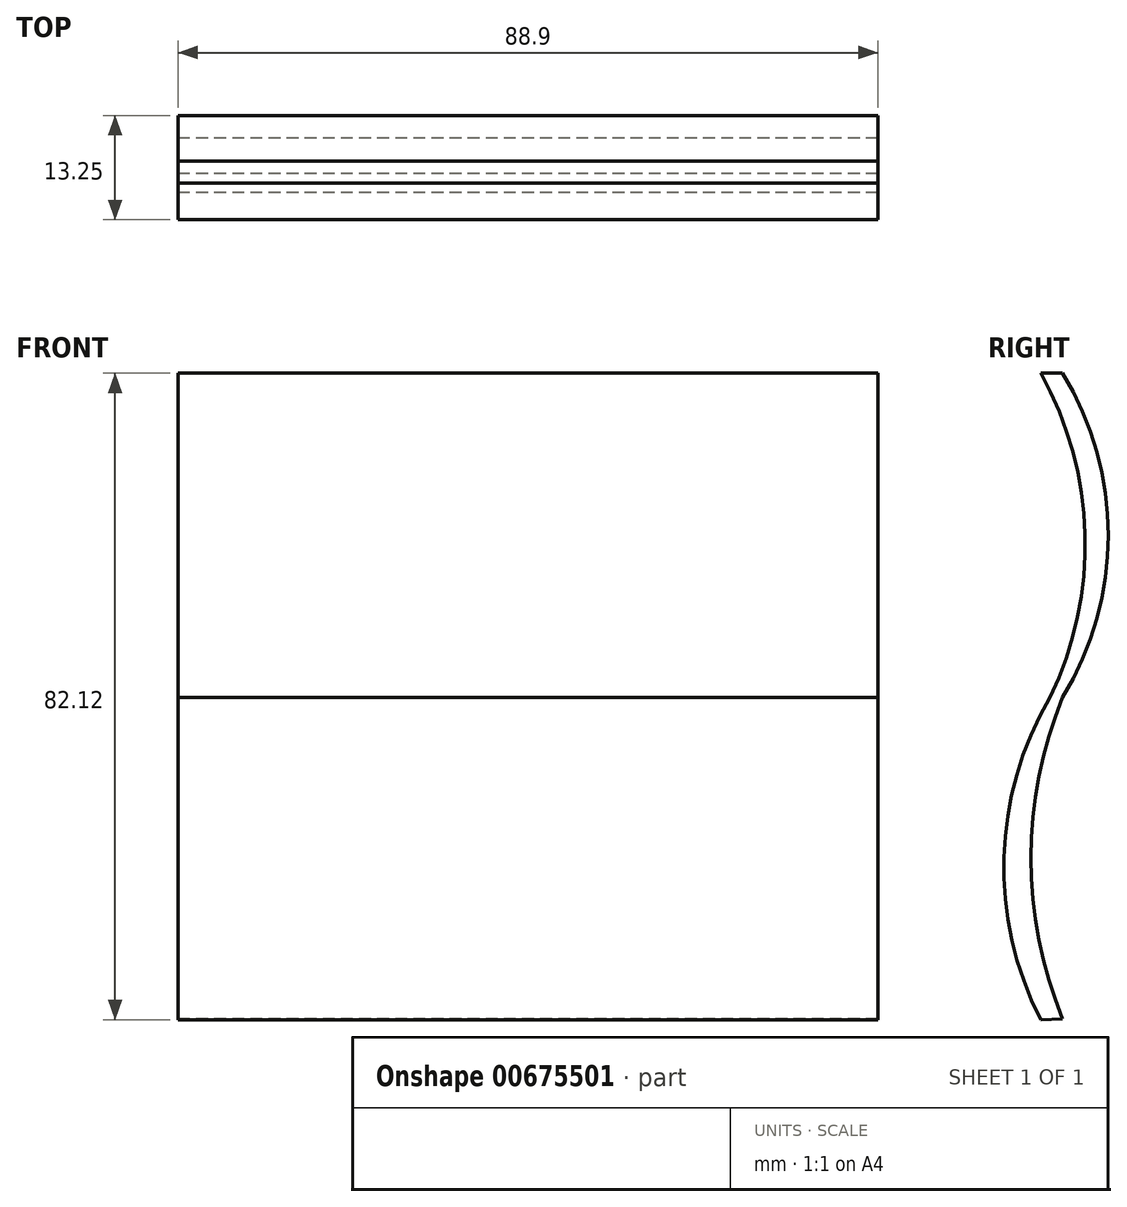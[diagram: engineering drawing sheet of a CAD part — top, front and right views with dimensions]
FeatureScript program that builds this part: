
annotation { "Feature Type Name" : "Feature", "Feature Type Description" : "" }
export const myFeature = defineFeature(function(context is Context, id is Id, definition is map)
    precondition{}
    {
        {
            var Q0;
            Q0=qCreatedBy(makeId("Right.planeOp"),FACE);
            var sketch = newSketch(context, id + "F0", { "sketchPlane" : qUnion([Q0])});
            skArc(sketch, "E0", {"start": v(0, 0) * mm, "mid": v(-3.98, -20.44) * mm, "end": v(0, -40.88) * mm});
            skArc(sketch, "E1", {"start": v(0, 0) * mm, "mid": v(5.8, 20.58) * mm, "end": v(0, 41.16) * mm});
            skLineSegment(sketch, "E2", {"start": v(0, 41.16) * mm, "end": v(-2.77, 41.16) * mm});
            skArc(sketch, "E3", {"start": v(-1.59, 0) * mm, "mid": v(2.87, 20.72) * mm, "end": v(-2.77, 41.16) * mm});
            skArc(sketch, "E4", {"start": v(-1.59, 0) * mm, "mid": v(-7.43, -20.33) * mm, "end": v(-2.77, -40.96) * mm});
            skLineSegment(sketch, "E5", {"start": v(0, -40.88) * mm, "end": v(-2.77, -40.96) * mm});
            skSolve(sketch);
        }
        {
            var Q0;
            Q0 = qSketchRegion(id + "F0", true);
            extrude(context, id + "F1", {"entities" : qUnion([Q0]), "depth" : 88.9 * mm, "offsetDistance" : 25.4 * mm});
        }
    });
